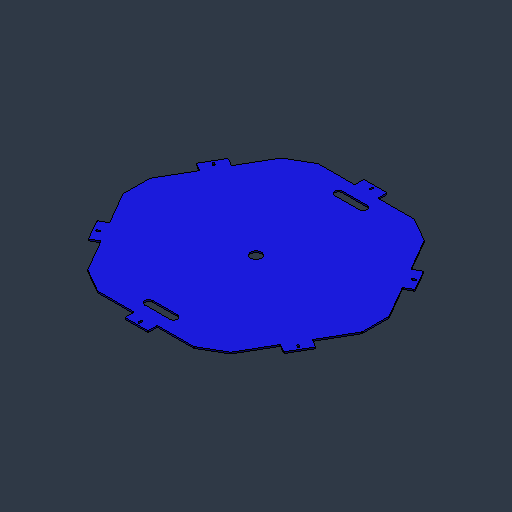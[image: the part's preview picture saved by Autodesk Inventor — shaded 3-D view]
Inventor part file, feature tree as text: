
AUTODESK INVENTOR PART (.ipt)
format: ipt  version: 2024.3 (Build 283343000, 343)  size: 161,280 bytes
history: native  units: mm (DEFAULTED — no unit token found)
features: fillet x1
ambient origin geometry x8: Origin, YZ Plane, XZ Plane, XY Plane, X Axis, Y Axis, Z Axis, Center Point
bodies: Solid1 (feature_tree)
feature tree (1):
  fillet  "Fillet2"  [1 undecoded]
note: 1 required parameter value undecoded (feature->parameter linkage not recoverable at this tier; creation-order binding heuristic only, values carry confidence <= 0.55)
